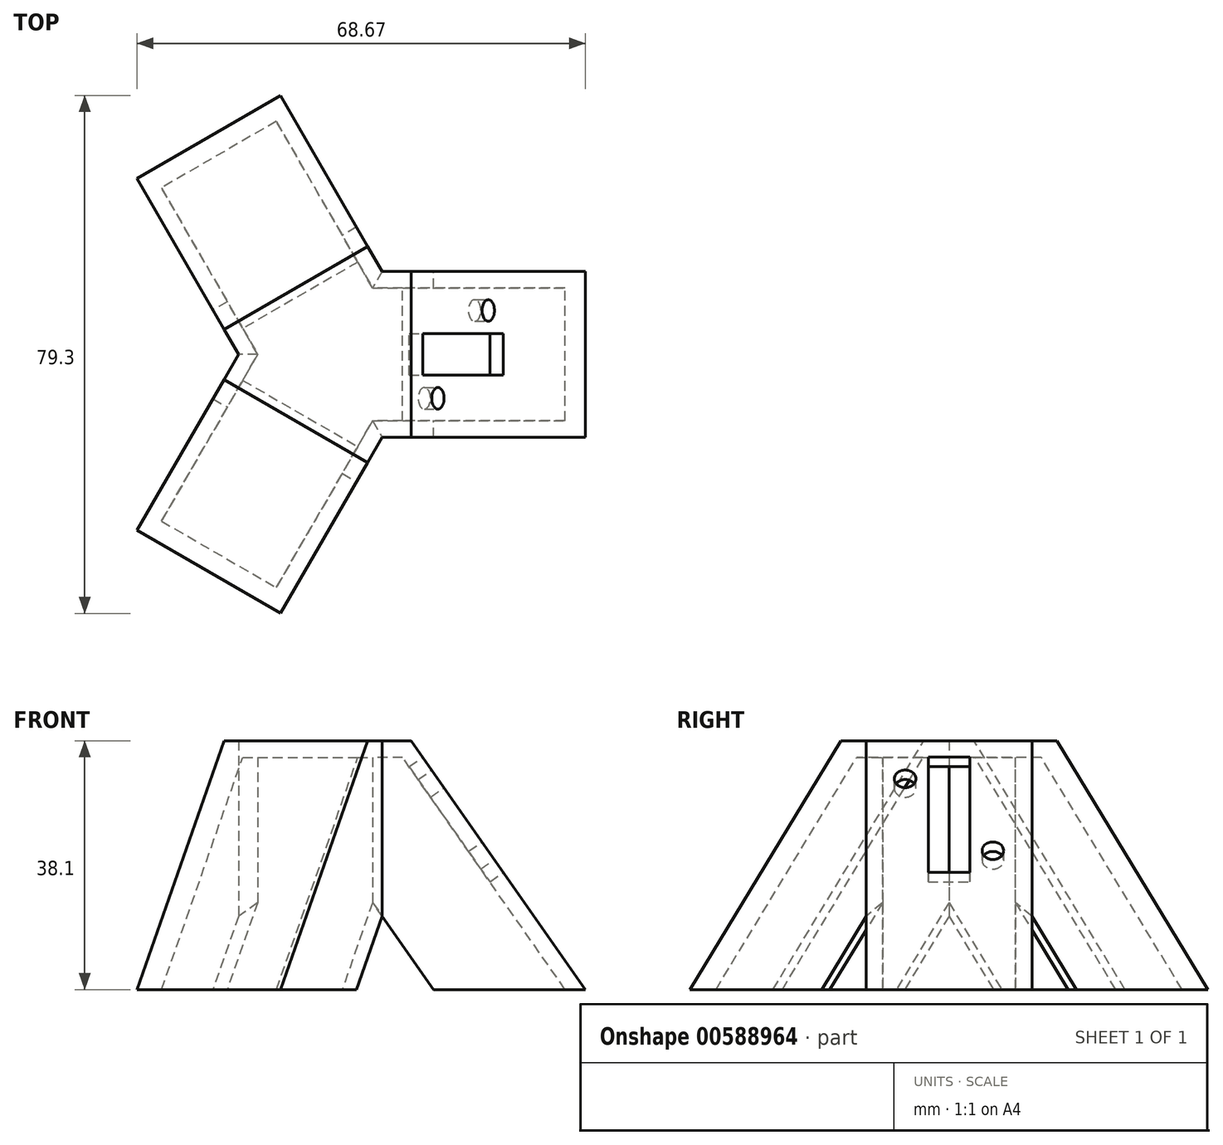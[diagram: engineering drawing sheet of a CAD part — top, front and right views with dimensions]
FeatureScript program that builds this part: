
annotation { "Feature Type Name" : "Feature", "Feature Type Description" : "" }
export const myFeature = defineFeature(function(context is Context, id is Id, definition is map)
    precondition{}
    {
        {
            var Q0;
            Q0=qCreatedBy(makeId("Front.planeOp"),FACE);
            var sketch = newSketch(context, id + "F0", { "sketchPlane" : qUnion([Q0])});
            skLineSegment(sketch, "E0", {"start": v(0, 0) * mm, "end": v(0, -38.1) * mm});
            skLineSegment(sketch, "E1", {"start": v(0, -38.1) * mm, "end": v(38.45, -38.1) * mm});
            skLineSegment(sketch, "E2", {"start": v(38.45, -38.1) * mm, "end": v(11.77, 0) * mm});
            skLineSegment(sketch, "E3", {"start": v(11.77, 0) * mm, "end": v(0, 0) * mm});
            skLineSegment(sketch, "E4", {"start": v(0, -16.4) * mm, "end": v(15.2, -38.1) * mm});
            skSolve(sketch);
        }
        {
            var Q0;
            {var subQ0=sQuery(id+"F0.wireOp",EDGE,"E2");Q0=makeQuery(id+"F0.imprint","IMPRINT",FACE,{"disambiguationData":[TD([[makeQuery(id+"F0.imprint","IMPRINT",EDGE,{"derivedFrom":subQ0}),1.0]])]});}
            extrude(context, id + "F1", {"entities" : qUnion([Q0]), "endBound" : BoundingType.SYMMETRIC, "depth" : 25.4 * mm, "offsetDistance" : 25.4 * mm});
        }
        {
            var Q0;
            Q0=makeQuery(id+"F1.opExtrude","SWEPT_FACE",FACE,{"disambiguationData":[OSD([sQuery(id+"F0.wireOp",EDGE,"E0")])]});
            var sketch = newSketch(context, id + "F2", { "sketchPlane" : qUnion([Q0])});
            skLineSegment(sketch, "E5", {"start": v(0, 0) * mm, "end": v(0, -16.4) * mm});
            skSolve(sketch);
        }
        {
            var Q0;
            Q0=makeQuery(id+"F1.opExtrude","SWEPT_BODY",BODY,{"disambiguationData":[OSD([sQuery(id+"F0.wireOp",EDGE,"E0"),sQuery(id+"F0.wireOp",EDGE,"E1"),sQuery(id+"F0.wireOp",EDGE,"E2"),sQuery(id+"F0.wireOp",EDGE,"E3"),sQuery(id+"F0.wireOp",EDGE,"E4")])]});
            var Q1;
            Q1=sQuery(id+"F2.wireOp",EDGE,"E5");
            circularPattern(context, id + "F3", {"operationType" : NewBodyOperationType.ADD, "entities" : qUnion([Q0]), "axis" : qUnion([Q1]), "angle" : 360 * degree, "instanceCount" : 3, "equalSpace" : true});
        }
        {
            var Q0;
            Q0=makeQuery(id+"F3.opPattern","COPY",FACE,{"derivedFrom":makeQuery(id+"F1.opExtrude","SWEPT_FACE",FACE,{"disambiguationData":[OSD([sQuery(id+"F0.wireOp",EDGE,"E1")])]}),"instanceName":"1"});
            var Q1;
            Q1=makeQuery(id+"F3.opPattern","COPY",FACE,{"derivedFrom":makeQuery(id+"F1.opExtrude","SWEPT_FACE",FACE,{"disambiguationData":[OSD([sQuery(id+"F0.wireOp",EDGE,"E4")])]}),"instanceName":"1"});
            var Q2;
            Q2=makeQuery(id+"F3.opPattern","COPY",FACE,{"derivedFrom":makeQuery(id+"F1.opExtrude","SWEPT_FACE",FACE,{"disambiguationData":[OSD([sQuery(id+"F0.wireOp",EDGE,"E4")])]}),"instanceName":"2"});
            var Q3;
            Q3=makeQuery(id+"F3.opPattern","COPY",FACE,{"derivedFrom":makeQuery(id+"F1.opExtrude","SWEPT_FACE",FACE,{"disambiguationData":[OSD([sQuery(id+"F0.wireOp",EDGE,"E1")])]}),"instanceName":"2"});
            var Q4;
            Q4=makeQuery(id+"F1.opExtrude","SWEPT_FACE",FACE,{"disambiguationData":[OSD([sQuery(id+"F0.wireOp",EDGE,"E4")])]});
            var Q5;
            Q5=makeQuery(id+"F1.opExtrude","SWEPT_FACE",FACE,{"disambiguationData":[OSD([sQuery(id+"F0.wireOp",EDGE,"E1")])]});
            shell(context, id + "F4", {"entities" : qUnion([Q0, Q1, Q2, Q3, Q4, Q5]), "thickness" : 2.54 * mm});
        }
        {
            var Q0;
            Q0=makeQuery(id+"F1.opExtrude","SWEPT_FACE",FACE,{"disambiguationData":[OSD([sQuery(id+"F0.wireOp",EDGE,"E2")])]});
            var sketch = newSketch(context, id + "F5", { "sketchPlane" : qUnion([Q0])});
            skCircle(sketch, "E6", {"center": v(-6.72, -13.88) * mm, "radius": 1.65 * mm});
            skCircle(sketch, "E7", {"center": v(6.72, -27.31) * mm, "radius": 1.65 * mm});
            skLineSegment(sketch, "E8.bottom", {"start": v(-6.72, -13.88) * mm, "end": v(6.72, -13.88) * mm, "construction": true});
            skLineSegment(sketch, "E8.top", {"start": v(-6.72, -27.31) * mm, "end": v(6.72, -27.31) * mm, "construction": true});
            skLineSegment(sketch, "E8.left", {"start": v(-6.72, -13.88) * mm, "end": v(-6.72, -27.31) * mm, "construction": true});
            skLineSegment(sketch, "E8.right", {"start": v(6.72, -13.88) * mm, "end": v(6.72, -27.31) * mm, "construction": true});
            skLineSegment(sketch, "E9.0.0", {"start": v(12.7, -53.26) * mm, "end": v(12.7, -6.75) * mm});
            skLineSegment(sketch, "E9.0.1", {"start": v(12.7, -6.75) * mm, "end": v(-12.7, -6.75) * mm});
            skLineSegment(sketch, "E9.0.2", {"start": v(-12.7, -6.75) * mm, "end": v(-12.7, -53.26) * mm});
            skLineSegment(sketch, "E9.0.3", {"start": v(-12.7, -53.26) * mm, "end": v(12.7, -53.26) * mm});
            skCircle(sketch, "E10", {"center": v(0, -20.6) * mm, "radius": 13.84 * mm, "construction": true});
            skLineSegment(sketch, "E11", {"start": v(0, -20.6) * mm, "end": v(0, -6.75) * mm, "construction": true});
            skLineSegment(sketch, "E12", {"start": v(6.72, -20.6) * mm, "end": v(0, -20.6) * mm, "construction": true});
            skLineSegment(sketch, "E13", {"start": v(0, -20.6) * mm, "end": v(0, -13.88) * mm, "construction": true});
            skLineSegment(sketch, "E14.bottom", {"start": v(-3.18, -9.82) * mm, "end": v(3.17, -9.82) * mm});
            skLineSegment(sketch, "E14.top", {"start": v(-3.18, -31.36) * mm, "end": v(3.17, -31.36) * mm});
            skLineSegment(sketch, "E14.left", {"start": v(-3.18, -9.82) * mm, "end": v(-3.18, -31.36) * mm});
            skLineSegment(sketch, "E14.right", {"start": v(3.17, -9.82) * mm, "end": v(3.17, -31.36) * mm});
            skLineSegment(sketch, "E15", {"start": v(0, -20.6) * mm, "end": v(0, -9.82) * mm, "construction": true});
            skLineSegment(sketch, "E16", {"start": v(3.17, -20.6) * mm, "end": v(0, -20.6) * mm, "construction": true});
            skSolve(sketch);
        }
        {
            var Q0;
            Q0=makeQuery(id+"F5.imprint","IMPRINT",FACE,{"disambiguationData":[TD([[makeQuery(id+"F5.imprint","IMPRINT",EDGE,{"derivedFrom":sQuery(id+"F5.wireOp",EDGE,"E14.bottom")}),-1.0]])]});
            var Q1;
            Q1=makeQuery(id+"F5.imprint","IMPRINT",FACE,{"disambiguationData":[TD([[makeQuery(id+"F5.imprint","IMPRINT",EDGE,{"derivedFrom":sQuery(id+"F5.wireOp",EDGE,"E7")}),1.0]])]});
            var Q2;
            Q2=makeQuery(id+"F5.imprint","IMPRINT",FACE,{"disambiguationData":[TD([[makeQuery(id+"F5.imprint","IMPRINT",EDGE,{"derivedFrom":sQuery(id+"F5.wireOp",EDGE,"E6")}),1.0]])]});
            extrude(context, id + "F6", {"entities" : qUnion([Q0, Q1, Q2]), "operationType" : NewBodyOperationType.REMOVE, "oppositeDirection" : true, "depth" : 2.54 * mm, "offsetDistance" : 25.4 * mm});
        }
    });
